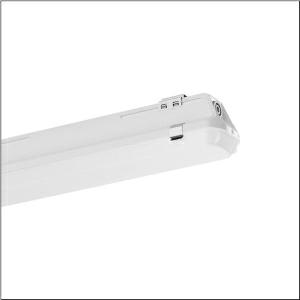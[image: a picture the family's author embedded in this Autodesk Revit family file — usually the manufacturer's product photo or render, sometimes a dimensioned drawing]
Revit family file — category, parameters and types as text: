
# Revit family: monsun_r__21_51fb207p480b_726c
name_source: partatom
category: Lighting Fixtures
units: mm (PartAtom-declared; Revit-internal decimal feet)

## family parameters
Cut with Voids When Loaded = No
Host = Face
Light Source = No
Part Type = Normal
Room Calculation Point = No
Round Connector Dimension = Use Diameter
Shared = No

## types (1)
- Monsun® 21 (1 x LED, 7270 lm, 52.8 W, 4000K)
    Apparent Load = 53 VA
    CIE Flux Codes = 45 75 93 94 100
    Color Rendering = 80
    Color Temperature = 4000K
    Default Elevation = 1800 mm
    Description = Monsun® 21, damp-proof luminaire, chain hanger, primary optical cover: enclosure, of PC, light emission: direct distribution, primary light characteristic: symmetric, installation type: suspended mounting, surface-mounted, horizontal mounting, vertical mounting, LED, rated luminous flux: 7.270lm, luminous efficacy: 138lm/W, light colour: 840, colour temperature: 4000K, control gear: ECG, with terminal, 3-pole, max. 2.5mm², mains connection: 220..240V, AC, 50/60Hz, rated input power: 53W, housing, of glass-fibre reinforced polyester, uncoated, bright grey, incl. chain hanger, length: 1.590mm, width: 90mm, height: 88mm, clip for enclosure, of stainless steel (V2A), ceiling mounting element, of stainless steel (V2A), chain hanger, of stainless steel (V2A), protection rating (complete): IP66, insulation class (complete): insulation class I (protective earthing), certification: CE, ENEC, VDE, UKCA, protection symbol: D, impact resistance: IK08, permissible operating ambient temperature: -25..+35°C, standard: EN 50419, EN 60598-2-1, corresponds to IFS (International Featured Standards) requirements for safety and quality in the food industry, for indoor or canopied outdoor use, no direct snow, no direct sun, no direct rain, contact your sales advisor before using the luminaires in applications with unclear chemical exposure, large temperature fluctuations or condensation-forming humidity, LABS conformity tested according to VDMA 24364:2018-05, packaging unit: 1 piece
    Height = 89 mm
    Lamp = 1 x LED
    Lamp Light Flux = 7270 lm
    Lamp Power = 52.8 W
    Lamp count = 1
    Length = 1590 mm
    Luminous efficacy = 138 lm/W
    Manufacturer = Siteco
    ModVariant = No
    Model = 51FB207P480B
    Mounting Place = Ceiling
    Mounting Type = Surface mounted
    Number of Poles = 1
    OnlyDefault = Yes
    Power Factor = 1
    Product Name = Monsun® 21
    Product group = damp-proof luminaire
    ProductGroupID = 301
    Protection Class = Protection class I
    Protection Degree = IP 66
    RLX_Detail_Level = 1
    RLX_Emergency_Light_Flux = 0 lm
    RLX_Emergency_Type = 0
    RLX_Emergency_Type_DB = No
    RlxData = <blob elided: 88549 chars, md5=0306e416>
    Socket = socket
    Standby Power = 0 W
    System Light Flux = 7270 lm
    System Power = 53 W
    Type Comments = Product without accessories
    Type Image = l_1006717.jpg
    URL = http://relux.com
    VarID = ---
    Voltage = 0 V
    Weight = 0.00 kg
    Width = 90 mm

## geometry (parser evidence)
native form markers: Blend x4, Sweep x15
no freeform markers — native parametric forms only
